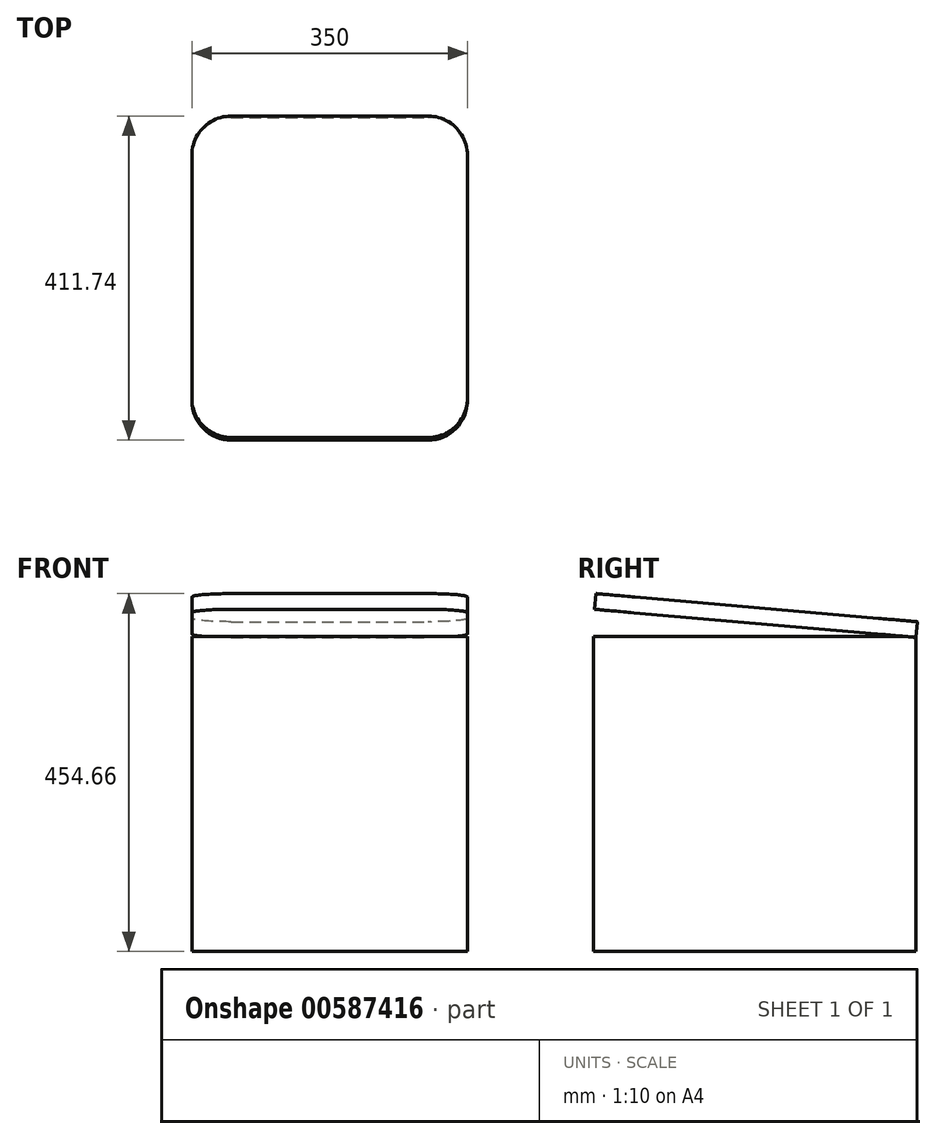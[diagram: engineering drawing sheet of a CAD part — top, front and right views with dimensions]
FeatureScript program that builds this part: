
annotation { "Feature Type Name" : "Feature", "Feature Type Description" : "" }
export const myFeature = defineFeature(function(context is Context, id is Id, definition is map)
    precondition{}
    {
        {
            var Q0;
            Q0=qCreatedBy(makeId("Top.planeOp"),FACE);
            var sketch = newSketch(context, id + "F0", { "sketchPlane" : qUnion([Q0])});
            skLineSegment(sketch, "E0.bottom", {"start": v(-175, -205) * mm, "end": v(175, -205) * mm});
            skLineSegment(sketch, "E0.top", {"start": v(-175, 205) * mm, "end": v(175, 205) * mm});
            skLineSegment(sketch, "E0.left", {"start": v(-175, -205) * mm, "end": v(-175, 205) * mm});
            skLineSegment(sketch, "E0.right", {"start": v(175, -205) * mm, "end": v(175, 205) * mm});
            skPoint(sketch, "E0.middle", {"position": v(0, 0) * mm});
            skSolve(sketch);
        }
        {
            var Q0;
            Q0 = qSketchRegion(id + "F0", true);
            extrude(context, id + "F1", {"entities" : qUnion([Q0]), "depth" : 400 * mm, "offsetDistance" : 25 * mm});
        }
        {
            var Q0;
            Q0=makeQuery(id+"F1.opExtrude","SWEPT_EDGE",EDGE,{"disambiguationData":[OSD([sQuery(id+"F0.wireOp",EDGE,"E0.bottom"),sQuery(id+"F0.wireOp",EDGE,"E0.left")])]});
            var Q1;
            Q1=makeQuery(id+"F1.opExtrude","SWEPT_EDGE",EDGE,{"disambiguationData":[OSD([sQuery(id+"F0.wireOp",EDGE,"E0.bottom"),sQuery(id+"F0.wireOp",EDGE,"E0.right")])]});
            var Q2;
            Q2=makeQuery(id+"F1.opExtrude","SWEPT_EDGE",EDGE,{"disambiguationData":[OSD([sQuery(id+"F0.wireOp",EDGE,"E0.top"),sQuery(id+"F0.wireOp",EDGE,"E0.right")])]});
            var Q3;
            Q3=makeQuery(id+"F1.opExtrude","SWEPT_EDGE",EDGE,{"disambiguationData":[OSD([sQuery(id+"F0.wireOp",EDGE,"E0.top"),sQuery(id+"F0.wireOp",EDGE,"E0.left")])]});
            fillet(context, id + "F2", {"entities" : qUnion([Q0, Q1, Q2, Q3]), "radius" : 50 * mm, "tangentPropagation" : true, "allowEdgeOverflow" : false});
        }
        {
            var Q0;
            Q0=makeQuery(id+"F1.opExtrude","CAP_FACE",FACE,{"disambiguationData":[OSD([sQuery(id+"F0.wireOp",EDGE,"E0.bottom"),sQuery(id+"F0.wireOp",EDGE,"E0.top"),sQuery(id+"F0.wireOp",EDGE,"E0.left"),sQuery(id+"F0.wireOp",EDGE,"E0.right")])],"isStart":false});
            extrude(context, id + "F3", {"entities" : qUnion([Q0]), "depth" : 20 * mm, "offsetDistance" : 25 * mm});
        }
        {
            var Q0;
            Q0=makeQuery(id+"F3.opExtrude","SWEPT_BODY",BODY,{"disambiguationData":[OSD([sQuery(id+"F0.wireOp",EDGE,"E0.bottom"),sQuery(id+"F0.wireOp",EDGE,"E0.top"),sQuery(id+"F0.wireOp",EDGE,"E0.left"),sQuery(id+"F0.wireOp",EDGE,"E0.right")])]});
            var Q1;
            Q1=makeQuery(id+"F1.opExtrude","CAP_EDGE",EDGE,{"disambiguationData":[OSD([sQuery(id+"F0.wireOp",EDGE,"E0.top")])],"isStart":false});
            transform(context, id + "F4", {"entities" : qUnion([Q0]), "transformType" : TransformType.ROTATION, "transformAxis" : qUnion([Q1]), "angle" : 5 * degree, "oppositeDirection" : true, "makeCopy" : false});
        }
        {
            var Q0;
            Q0=makeQuery(id+"F3.opExtrude","SWEPT_BODY",BODY,{"disambiguationData":[OSD([sQuery(id+"F0.wireOp",EDGE,"E0.bottom"),sQuery(id+"F0.wireOp",EDGE,"E0.top"),sQuery(id+"F0.wireOp",EDGE,"E0.left"),sQuery(id+"F0.wireOp",EDGE,"E0.right")])]});
            transform(context, id + "F5", {"entities" : qUnion([Q0]), "transformType" : TransformType.TRANSLATION_3D, "dx" : 0 * mm, "dy" : 0 * mm, "dz" : -1 * mm, "makeCopy" : false});
        }
    });
